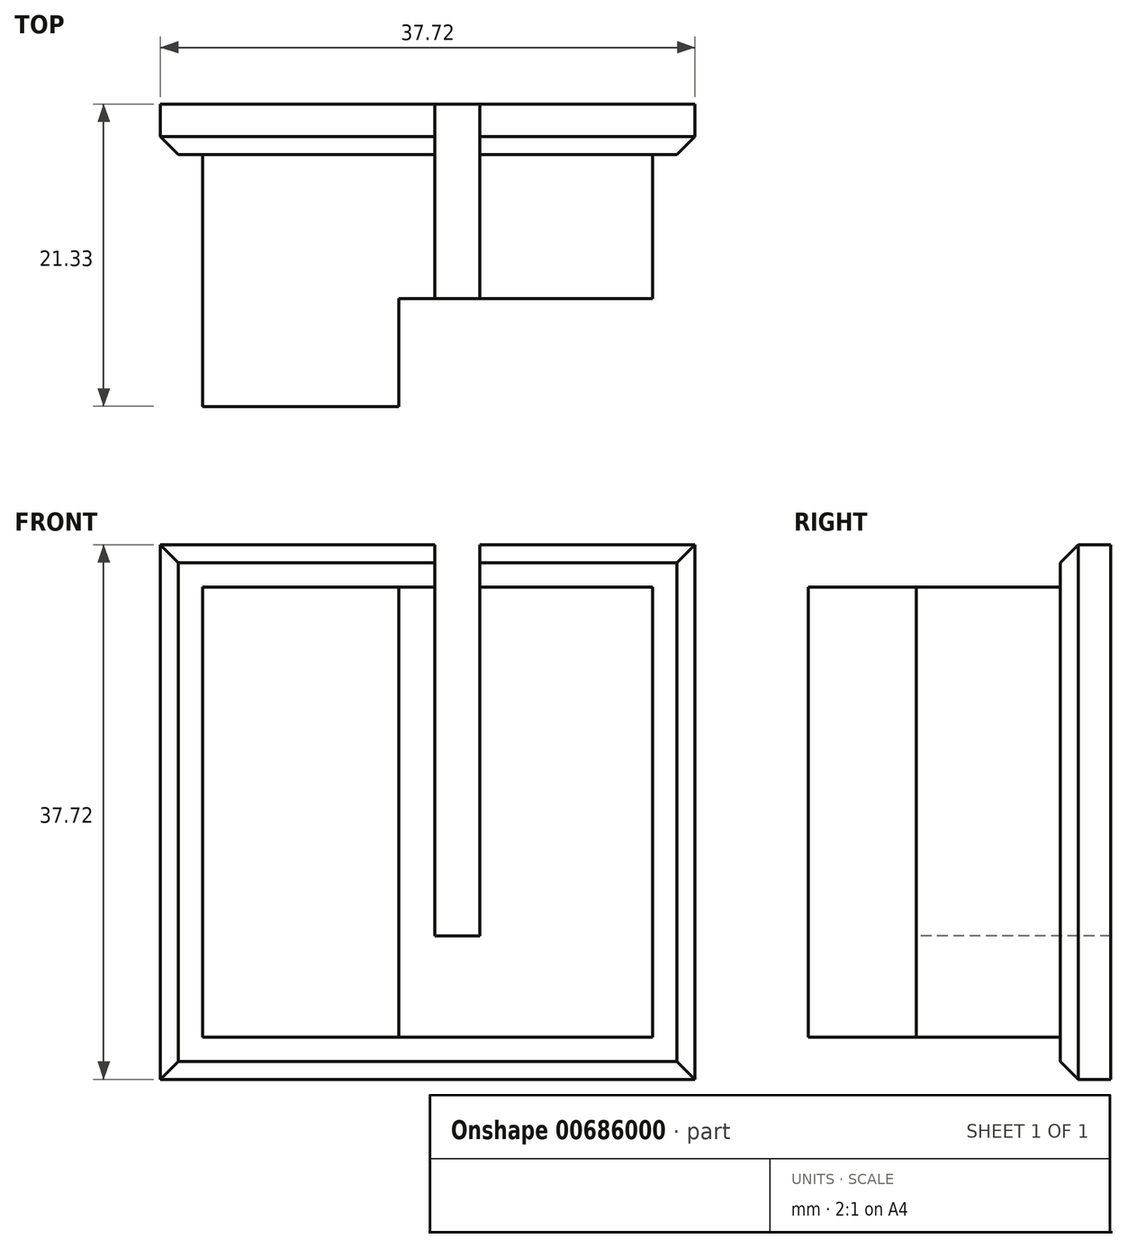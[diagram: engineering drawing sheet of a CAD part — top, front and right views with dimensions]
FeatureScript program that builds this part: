
annotation { "Feature Type Name" : "Feature", "Feature Type Description" : "" }
export const myFeature = defineFeature(function(context is Context, id is Id, definition is map)
    precondition{}
    {
        {
            var Q0;
            Q0=qCreatedBy(makeId("Front.planeOp"),FACE);
            var sketch = newSketch(context, id + "F0", { "sketchPlane" : qUnion([Q0])});
            skLineSegment(sketch, "E0.bottom", {"start": v(18.86, -18.86) * mm, "end": v(-18.86, -18.86) * mm});
            skLineSegment(sketch, "E0.top", {"start": v(18.86, 18.86) * mm, "end": v(-18.86, 18.86) * mm});
            skLineSegment(sketch, "E0.left", {"start": v(18.86, -18.86) * mm, "end": v(18.86, 18.86) * mm});
            skLineSegment(sketch, "E0.right", {"start": v(-18.86, -18.86) * mm, "end": v(-18.86, 18.86) * mm});
            skPoint(sketch, "E0.middle", {"position": v(0, 0) * mm});
            skSolve(sketch);
        }
        {
            var Q0;
            Q0=makeQuery(id+"F0.imprint","IMPRINT",FACE,{"disambiguationData":[TD([[makeQuery(id+"F0.imprint","IMPRINT",EDGE,{"derivedFrom":sQuery(id+"F0.wireOp",EDGE,"E0.bottom")}),-1.0]])]});
            extrude(context, id + "F1", {"entities" : qUnion([Q0]), "depth" : 2.8 * mm, "offsetDistance" : 25.4 * mm});
        }
        {
            var Q0;
            Q0=makeQuery(id+"F1.opExtrude","CAP_FACE",FACE,{"disambiguationData":[OSD([sQuery(id+"F0.wireOp",EDGE,"E0.bottom"),sQuery(id+"F0.wireOp",EDGE,"E0.top"),sQuery(id+"F0.wireOp",EDGE,"E0.left"),sQuery(id+"F0.wireOp",EDGE,"E0.right")])],"isStart":false});
            var sketch = newSketch(context, id + "F2", { "sketchPlane" : qUnion([Q0])});
            skLineSegment(sketch, "E1.bottom", {"start": v(15.88, -15.88) * mm, "end": v(-15.88, -15.88) * mm});
            skLineSegment(sketch, "E1.top", {"start": v(15.88, 15.88) * mm, "end": v(-15.88, 15.88) * mm});
            skLineSegment(sketch, "E1.left", {"start": v(15.88, -15.88) * mm, "end": v(15.88, 15.88) * mm});
            skLineSegment(sketch, "E1.right", {"start": v(-15.88, -15.88) * mm, "end": v(-15.88, 15.87) * mm});
            skPoint(sketch, "E1.middle", {"position": v(0, 0) * mm});
            skSolve(sketch);
        }
        {
            var Q0;
            Q0=makeQuery(id+"F2.imprint","IMPRINT",FACE,{"disambiguationData":[TD([[makeQuery(id+"F2.imprint","IMPRINT",EDGE,{"derivedFrom":sQuery(id+"F2.wireOp",EDGE,"E1.bottom")}),-1.0]])]});
            extrude(context, id + "F3", {"entities" : qUnion([Q0]), "operationType" : NewBodyOperationType.ADD, "depth" : 10.16 * mm, "offsetDistance" : 25.4 * mm});
        }
        {
            var Q0;
            Q0=makeQuery(id+"F1.opExtrude","CAP_EDGE",EDGE,{"disambiguationData":[OSD([sQuery(id+"F0.wireOp",EDGE,"E0.right")])],"isStart":false});
            var Q1;
            Q1=makeQuery(id+"F1.opExtrude","CAP_EDGE",EDGE,{"disambiguationData":[OSD([sQuery(id+"F0.wireOp",EDGE,"E0.bottom")])],"isStart":false});
            var Q2;
            Q2=makeQuery(id+"F1.opExtrude","CAP_EDGE",EDGE,{"disambiguationData":[OSD([sQuery(id+"F0.wireOp",EDGE,"E0.left")])],"isStart":false});
            var Q3;
            Q3=makeQuery(id+"F1.opExtrude","CAP_EDGE",EDGE,{"disambiguationData":[OSD([sQuery(id+"F0.wireOp",EDGE,"E0.top")])],"isStart":false});
            chamfer(context, id + "F4", {"entities" : qUnion([Q0, Q1, Q2, Q3]), "width" : 1.27 * mm, "tangentPropagation" : true});
        }
        {
            var Q0;
            Q0=makeQuery(id+"F3.opExtrude","CAP_FACE",FACE,{"disambiguationData":[OSD([sQuery(id+"F2.wireOp",EDGE,"E1.bottom"),sQuery(id+"F2.wireOp",EDGE,"E1.top"),sQuery(id+"F2.wireOp",EDGE,"E1.left"),sQuery(id+"F2.wireOp",EDGE,"E1.right")])],"isStart":false});
            var sketch = newSketch(context, id + "F5", { "sketchPlane" : qUnion([Q0])});
            skLineSegment(sketch, "E2.bottom", {"start": v(-15.88, 15.87) * mm, "end": v(-2.03, 15.87) * mm});
            skLineSegment(sketch, "E2.top", {"start": v(-15.88, -15.88) * mm, "end": v(-2.03, -15.88) * mm});
            skLineSegment(sketch, "E2.left", {"start": v(-15.88, 15.87) * mm, "end": v(-15.88, -15.88) * mm});
            skLineSegment(sketch, "E2.right", {"start": v(-2.03, 15.87) * mm, "end": v(-2.03, -15.88) * mm});
            skSolve(sketch);
        }
        {
            var Q0;
            Q0=makeQuery(id+"F5.imprint","IMPRINT",FACE,{"disambiguationData":[TD([[makeQuery(id+"F5.imprint","IMPRINT",EDGE,{"derivedFrom":sQuery(id+"F5.wireOp",EDGE,"E2.bottom")}),1.0]])]});
            extrude(context, id + "F6", {"entities" : qUnion([Q0]), "operationType" : NewBodyOperationType.ADD, "depth" : 7.62 * mm, "offsetDistance" : 25.4 * mm});
        }
        {
            var Q0;
            Q0=makeQuery(id+"F3.opExtrude","CAP_FACE",FACE,{"disambiguationData":[OSD([sQuery(id+"F2.wireOp",EDGE,"E1.bottom"),sQuery(id+"F2.wireOp",EDGE,"E1.top"),sQuery(id+"F2.wireOp",EDGE,"E1.left"),sQuery(id+"F2.wireOp",EDGE,"E1.right")])],"isStart":false});
            var sketch = newSketch(context, id + "F7", { "sketchPlane" : qUnion([Q0])});
            skLineSegment(sketch, "E3.left", {"start": v(-2.03, -8.26) * mm, "end": v(-2.03, 6.98) * mm});
            skLineSegment(sketch, "E4.bottom", {"start": v(0.5, 15.88) * mm, "end": v(3.68, 15.88) * mm});
            skLineSegment(sketch, "E4.top", {"start": v(0.5, -8.73) * mm, "end": v(3.68, -8.73) * mm});
            skLineSegment(sketch, "E4.left", {"start": v(0.5, 15.88) * mm, "end": v(0.5, -8.73) * mm});
            skLineSegment(sketch, "E4.right", {"start": v(3.68, 15.88) * mm, "end": v(3.68, -8.73) * mm});
            skLineSegment(sketch, "E5.top", {"start": v(0.5, 18.96) * mm, "end": v(3.68, 18.96) * mm});
            skLineSegment(sketch, "E5.left", {"start": v(0.5, 15.88) * mm, "end": v(0.5, 18.96) * mm});
            skLineSegment(sketch, "E5.right", {"start": v(3.68, 15.88) * mm, "end": v(3.68, 18.96) * mm});
            skSolve(sketch);
        }
        {
            var Q0;
            Q0=makeQuery(id+"F7.imprint","IMPRINT",FACE,{"disambiguationData":[TD([[makeQuery(id+"F7.imprint","IMPRINT",EDGE,{"derivedFrom":sQuery(id+"F7.wireOp",EDGE,"E3.bottom")}),1.0]])]});
            var Q1;
            Q1=makeQuery(id+"F7.imprint","IMPRINT",FACE,{"disambiguationData":[TD([[makeQuery(id+"F7.imprint","IMPRINT",EDGE,{"derivedFrom":sQuery(id+"F7.wireOp",EDGE,"E4.bottom")}),1.0]])]});
            var Q2;
            Q2=makeQuery(id+"F7.imprint","IMPRINT",FACE,{"disambiguationData":[TD([[makeQuery(id+"F7.imprint","IMPRINT",EDGE,{"derivedFrom":sQuery(id+"F7.wireOp",EDGE,"E4.bottom")}),-1.0]])]});
            var Q3;
            Q3=makeQuery(id+"F7.imprint","IMPRINT",FACE,{"disambiguationData":[TD([[makeQuery(id+"F7.imprint","IMPRINT",EDGE,{"derivedFrom":sQuery(id+"F7.wireOp",EDGE,"E4.top")}),1.0]])]});
            extrude(context, id + "F8", {"entities" : qUnion([Q0, Q1, Q2, Q3]), "operationType" : NewBodyOperationType.REMOVE, "endBound" : BoundingType.THROUGH_ALL, "oppositeDirection" : true, "depth" : 25.4 * mm, "offsetDistance" : 25.4 * mm});
        }
        {
            var Q0;
            Q0=makeQuery(id+"F1.opExtrude","CAP_FACE",FACE,{"disambiguationData":[OSD([sQuery(id+"F0.wireOp",EDGE,"E0.bottom"),sQuery(id+"F0.wireOp",EDGE,"E0.top"),sQuery(id+"F0.wireOp",EDGE,"E0.left"),sQuery(id+"F0.wireOp",EDGE,"E0.right")])],"isStart":true});
            var sketch = newSketch(context, id + "F9", { "sketchPlane" : qUnion([Q0])});
            skLineSegment(sketch, "E6.bottom", {"start": v(-0.5, -8.73) * mm, "end": v(-3.66, -8.73) * mm});
            skLineSegment(sketch, "E6.top", {"start": v(-0.5, 18.86) * mm, "end": v(-3.66, 18.86) * mm});
            skLineSegment(sketch, "E6.left", {"start": v(-0.5, -8.73) * mm, "end": v(-0.5, 18.86) * mm});
            skLineSegment(sketch, "E6.right", {"start": v(-3.66, -8.73) * mm, "end": v(-3.66, 18.86) * mm});
            skSolve(sketch);
        }
        {
            var Q0;
            Q0=makeQuery(id+"F9.imprint","IMPRINT",FACE,{"disambiguationData":[TD([[makeQuery(id+"F9.imprint","IMPRINT",EDGE,{"derivedFrom":sQuery(id+"F9.wireOp",EDGE,"E6.bottom")}),-1.0]])]});
            extrude(context, id + "F10", {"entities" : qUnion([Q0]), "operationType" : NewBodyOperationType.REMOVE, "endBound" : BoundingType.THROUGH_ALL, "oppositeDirection" : true, "depth" : 25.4 * mm, "offsetDistance" : 25.4 * mm});
        }
        {
            var Q0;
            Q0=makeQuery(id+"F1.opExtrude","CAP_FACE",FACE,{"disambiguationData":[OSD([sQuery(id+"F0.wireOp",EDGE,"E0.bottom"),sQuery(id+"F0.wireOp",EDGE,"E0.top"),sQuery(id+"F0.wireOp",EDGE,"E0.left"),sQuery(id+"F0.wireOp",EDGE,"E0.right")])],"isStart":true});
            extrude(context, id + "F11", {"entities" : qUnion([Q0]), "operationType" : NewBodyOperationType.ADD, "depth" : 0.76 * mm, "offsetDistance" : 25.4 * mm});
        }
    });
